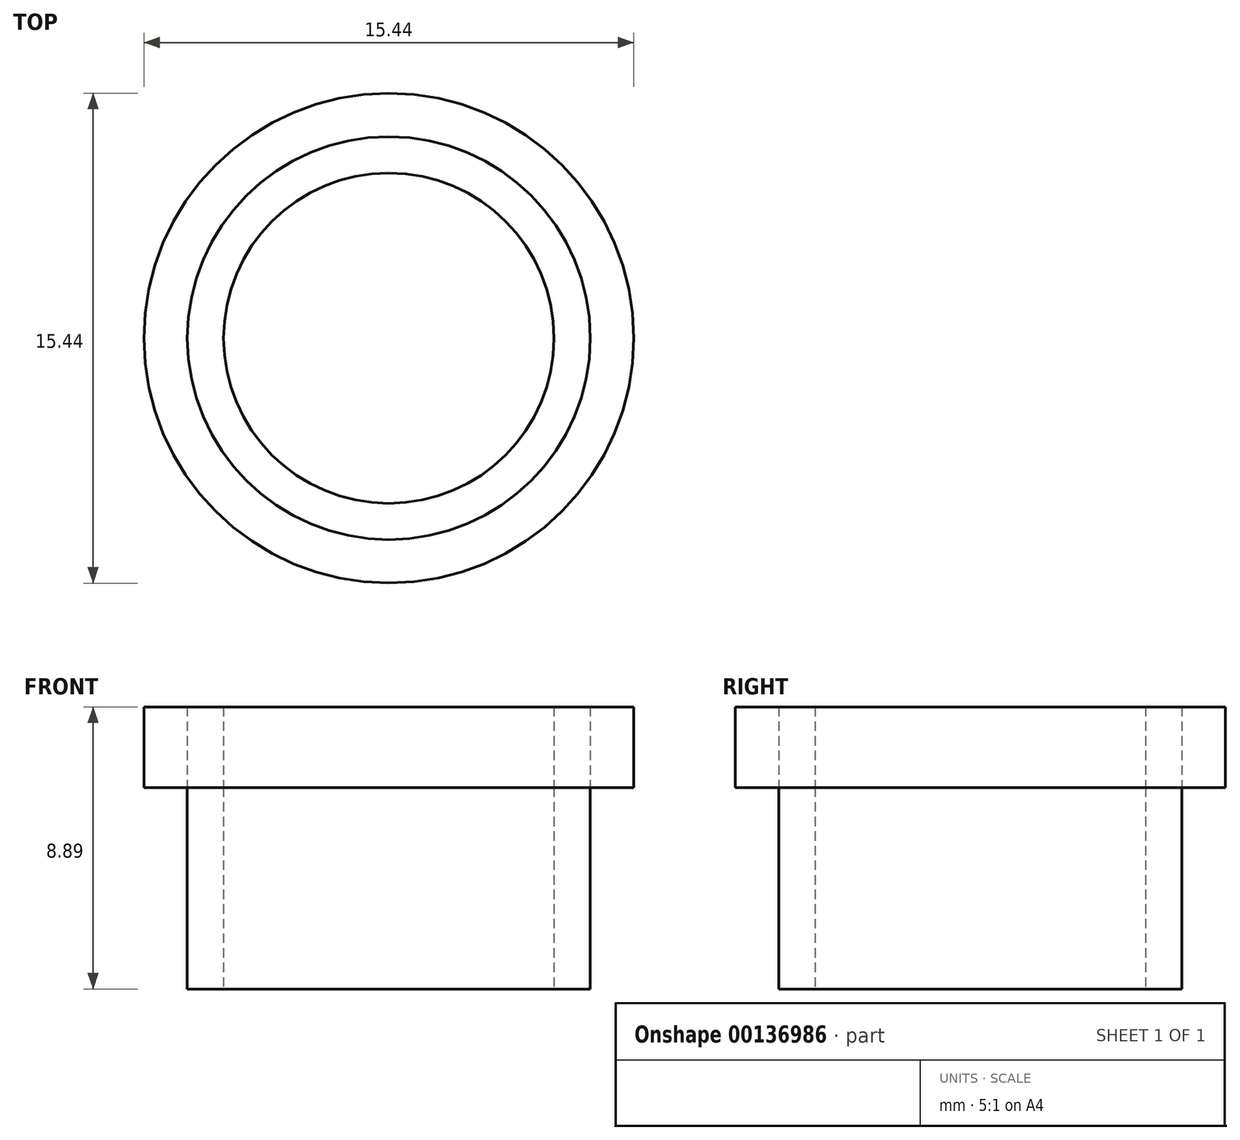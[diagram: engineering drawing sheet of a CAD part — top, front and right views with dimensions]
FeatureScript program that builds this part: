
annotation { "Feature Type Name" : "Feature", "Feature Type Description" : "" }
export const myFeature = defineFeature(function(context is Context, id is Id, definition is map)
    precondition{}
    {
        {
            var Q0;
            Q0=qCreatedBy(makeId("Top.planeOp"),FACE);
            var sketch = newSketch(context, id + "F0", { "sketchPlane" : qUnion([Q0])});
            skCircle(sketch, "E0", {"center": v(0, 0) * mm, "radius": 6.35 * mm});
            skCircle(sketch, "E1", {"center": v(0, 0) * mm, "radius": 5.2 * mm});
            skSolve(sketch);
        }
        {
            var Q0;
            Q0=makeQuery(id+"F0.imprint","IMPRINT",FACE,{"disambiguationData":[TD([[makeQuery(id+"F0.imprint","IMPRINT",EDGE,{"derivedFrom":sQuery(id+"F0.wireOp",EDGE,"E0")}),1.0]])]});
            extrude(context, id + "F1", {"entities" : qUnion([Q0]), "depth" : 6.35 * mm});
        }
        {
            var Q0;
            Q0=makeQuery(id+"F1.opExtrude","CAP_FACE",FACE,{"disambiguationData":[OSD([sQuery(id+"F0.wireOp",EDGE,"E0"),sQuery(id+"F0.wireOp",EDGE,"E1")])],"isStart":false});
            var sketch = newSketch(context, id + "F2", { "sketchPlane" : qUnion([Q0])});
            skCircle(sketch, "E2", {"center": v(0, 0) * mm, "radius": 7.72 * mm});
            skSolve(sketch);
        }
        {
            var Q0;
            Q0=makeQuery(id+"F2.imprint","IMPRINT",FACE,{"disambiguationData":[TD([[makeQuery(id+"F2.imprint","IMPRINT",EDGE,{"derivedFrom":sQuery(id+"F2.wireOp",EDGE,"E2")}),1.0]])]});
            extrude(context, id + "F3", {"entities" : qUnion([Q0]), "depth" : 2.54 * mm});
        }
        {
            var Q0;
            Q0=makeQuery(id+"F1.opExtrude","CAP_FACE",FACE,{"disambiguationData":[OSD([sQuery(id+"F0.wireOp",EDGE,"E0"),sQuery(id+"F0.wireOp",EDGE,"E1")])],"isStart":false});
            extrude(context, id + "F4", {"entities" : qUnion([Q0]), "depth" : 2.54 * mm});
        }
    });
